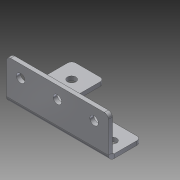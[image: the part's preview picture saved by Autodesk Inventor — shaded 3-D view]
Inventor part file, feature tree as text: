
AUTODESK INVENTOR PART (.ipt)
format: ipt  version: 2013 (Build 170138000, 138)  size: 221,696 bytes
history: native  units: in
note: dims shown in document units (in); Inventor stores cm internally (conversion verified against a paired STEP export)
features: sheet_metal_op x4, other x4, sketch x3, chamfer x1
ambient origin geometry x8: Origin, YZ Plane, XZ Plane, XY Plane, X Axis, Y Axis, Z Axis, Center Point
feature tree (12):
  sheet_metal_op  "Face1"
  sheet_metal_op  "Flange1"
  chamfer  "Corner Round1"
  sketch  "Sketch1"  dims[d0=2.0in]
  other  "Plate1"
  sketch  "Sketch2"  dims[d1=1.0in]
  other  "Plate2"
  sheet_metal_op  "Bend1"
  sheet_metal_op  "Corner1"
  sketch  "Sketch3"  dims[d2=0.26in d3=0.26in d4=1.0in d8=0.125in d9=0.125in d10=0.0625in d11=0.25in d12=0.125in d13=1.25in d14=90.0deg d15=0.05in d16=0.5in d17=0.125in d18=0.125in d19=0.26in d22=0.125in d23=0.0in d24=0.125in d25=2.125in d26=2.25in d27=0.75in d28=0.875in d29=2.25in d5=0.125in d6=0.0in]
  other  "Cut1"
  other  "Definition1"
